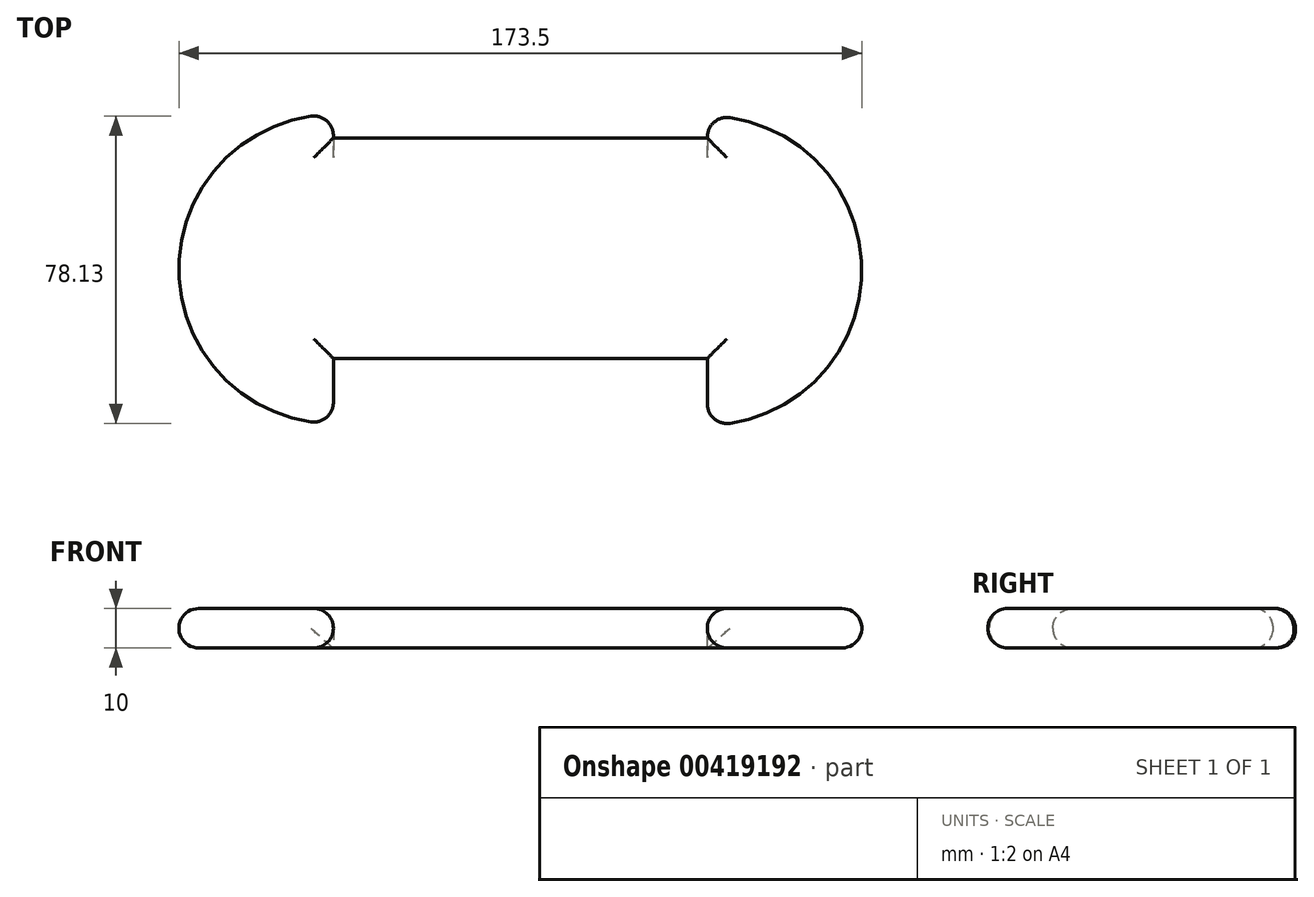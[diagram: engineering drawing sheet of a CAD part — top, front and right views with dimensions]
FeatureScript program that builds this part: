
annotation { "Feature Type Name" : "Feature", "Feature Type Description" : "" }
export const myFeature = defineFeature(function(context is Context, id is Id, definition is map)
    precondition{}
    {
        {
            var Q0;
            Q0=qCreatedBy(makeId("Top.planeOp"),FACE);
            var sketch = newSketch(context, id + "F0", { "sketchPlane" : qUnion([Q0])});
            skLineSegment(sketch, "E0.bottom", {"start": v(-45.33, 33.57) * mm, "end": v(49.67, 33.57) * mm});
            skLineSegment(sketch, "E0.top", {"start": v(-45.33, -22.43) * mm, "end": v(49.67, -22.43) * mm});
            skLineSegment(sketch, "E0.left", {"start": v(-45.33, 33.57) * mm, "end": v(-45.33, -22.43) * mm});
            skLineSegment(sketch, "E0.right", {"start": v(49.67, 33.57) * mm, "end": v(49.67, -22.43) * mm});
            skArc(sketch, "E1", {"start": v(-45.33, 39.54) * mm, "mid": v(-84.58, 0.3) * mm, "end": v(-45.33, -38.96) * mm});
            skArc(sketch, "E2", {"start": v(49.67, -39.32) * mm, "mid": v(88.92, -0.07) * mm, "end": v(49.67, 39.18) * mm});
            skLineSegment(sketch, "E3", {"start": v(-45.33, 33.57) * mm, "end": v(-45.33, 39.54) * mm});
            skLineSegment(sketch, "E4", {"start": v(-45.33, 39.54) * mm, "end": v(-45.33, -38.96) * mm});
            skLineSegment(sketch, "E5", {"start": v(49.67, 33.57) * mm, "end": v(49.67, 39.18) * mm});
            skLineSegment(sketch, "E6", {"start": v(49.67, 39.18) * mm, "end": v(49.67, -39.32) * mm});
            skSolve(sketch);
        }
        {
            var Q0;
            {var subQ0=sQuery(id+"F0.wireOp",EDGE,"E2");Q0=makeQuery(id+"F0.imprint","IMPRINT",FACE,{"disambiguationData":[TD([[makeQuery(id+"F0.imprint","IMPRINT",EDGE,{"derivedFrom":subQ0}),1.0]])]});}
            var Q1;
            {var subQ0=sQuery(id+"F0.wireOp",EDGE,"E0.bottom");Q1=makeQuery(id+"F0.imprint","IMPRINT",FACE,{"disambiguationData":[TD([[makeQuery(id+"F0.imprint","IMPRINT",EDGE,{"derivedFrom":subQ0}),-1.0]])]});}
            var Q2;
            {var subQ0=sQuery(id+"F0.wireOp",EDGE,"E1");Q2=makeQuery(id+"F0.imprint","IMPRINT",FACE,{"disambiguationData":[TD([[makeQuery(id+"F0.imprint","IMPRINT",EDGE,{"derivedFrom":subQ0}),1.0]])]});}
            extrude(context, id + "F1", {"entities" : qUnion([Q0, Q1, Q2]), "depth" : 10 * mm});
        }
        {
            var Q0;
            Q0=makeQuery(id+"F1.opExtrude","CAP_EDGE",EDGE,{"disambiguationData":[OSD([sQuery(id+"F0.wireOp",EDGE,"E1")])],"isStart":true});
            var Q1;
            Q1=makeQuery(id+"F1.opExtrude","CAP_EDGE",EDGE,{"disambiguationData":[OSD([sQuery(id+"F0.wireOp",EDGE,"E0.top")])],"isStart":true});
            var Q2;
            {var subQ0=sQuery(id+"F0.wireOp",EDGE,"E6");Q2=makeQuery(id+"F1.opExtrude","CAP_EDGE",EDGE,{"disambiguationData":[OSD([subQ0]),TDD([makeQuery(id+"F0.imprint","IMPRINT",EDGE,{"disambiguationData":[TD([[makeQuery(id+"F0.imprint","INTERSECT",VERTEX,{"derivedFrom":[sQuery(id+"F0.wireOp",EDGE,"E0.top"),subQ0]}),-1.0]])],"derivedFrom":subQ0})])],"isStart":true});}
            var Q3;
            Q3=makeQuery(id+"F1.opExtrude","CAP_EDGE",EDGE,{"disambiguationData":[OSD([sQuery(id+"F0.wireOp",EDGE,"E2")])],"isStart":true});
            var Q4;
            {var subQ0=sQuery(id+"F0.wireOp",EDGE,"E6");Q4=makeQuery(id+"F1.opExtrude","CAP_EDGE",EDGE,{"disambiguationData":[OSD([subQ0]),TDD([makeQuery(id+"F0.imprint","IMPRINT",EDGE,{"disambiguationData":[TD([[makeQuery(id+"F0.imprint","INTERSECT",VERTEX,{"derivedFrom":[sQuery(id+"F0.wireOp",EDGE,"E0.bottom"),subQ0]}),1.0]])],"derivedFrom":subQ0})])],"isStart":true});}
            var Q5;
            Q5=makeQuery(id+"F1.opExtrude","CAP_EDGE",EDGE,{"disambiguationData":[OSD([sQuery(id+"F0.wireOp",EDGE,"E0.bottom")])],"isStart":true});
            var Q6;
            {var subQ0=sQuery(id+"F0.wireOp",EDGE,"E4");Q6=makeQuery(id+"F1.opExtrude","CAP_EDGE",EDGE,{"disambiguationData":[OSD([subQ0]),TDD([makeQuery(id+"F0.imprint","IMPRINT",EDGE,{"disambiguationData":[TD([[makeQuery(id+"F0.imprint","INTERSECT",VERTEX,{"derivedFrom":[sQuery(id+"F0.wireOp",EDGE,"E0.bottom"),subQ0]}),1.0]])],"derivedFrom":subQ0})])],"isStart":true});}
            var Q7;
            {var subQ0=sQuery(id+"F0.wireOp",EDGE,"E6");var subQ1=sQuery(id+"F0.wireOp",EDGE,"E2");Q7=makeQuery(id+"F1.opExtrude","SWEPT_EDGE",EDGE,{"disambiguationData":[OSD([subQ1,subQ0]),TDD([makeQuery(id+"F0.imprint","INTERSECT",VERTEX,{"disambiguationData":[OD(0.0)],"derivedFrom":[subQ1,subQ0]})])]});}
            var Q8;
            Q8=makeQuery(id+"F1.opExtrude","CAP_EDGE",EDGE,{"disambiguationData":[OSD([sQuery(id+"F0.wireOp",EDGE,"E2")])],"isStart":false});
            var Q9;
            {var subQ0=sQuery(id+"F0.wireOp",EDGE,"E4");var subQ1=sQuery(id+"F0.wireOp",EDGE,"E1");Q9=makeQuery(id+"F1.opExtrude","SWEPT_EDGE",EDGE,{"disambiguationData":[OSD([subQ1,subQ0]),TDD([makeQuery(id+"F0.imprint","INTERSECT",VERTEX,{"disambiguationData":[OD(1.0)],"derivedFrom":[subQ1,subQ0]})])]});}
            var Q10;
            Q10=makeQuery(id+"F1.opExtrude","CAP_EDGE",EDGE,{"disambiguationData":[OSD([sQuery(id+"F0.wireOp",EDGE,"E1")])],"isStart":false});
            var Q11;
            Q11=makeQuery(id+"F1.opExtrude","CAP_EDGE",EDGE,{"disambiguationData":[OSD([sQuery(id+"F0.wireOp",EDGE,"E0.top")])],"isStart":false});
            var Q12;
            Q12=makeQuery(id+"F1.opExtrude","SWEPT_FACE",FACE,{"disambiguationData":[OSD([sQuery(id+"F0.wireOp",EDGE,"E2")])]});
            var Q13;
            Q13=makeQuery(id+"F1.opExtrude","SWEPT_FACE",FACE,{"disambiguationData":[OSD([sQuery(id+"F0.wireOp",EDGE,"E1")])]});
            var Q14;
            {var subQ0=sQuery(id+"F0.wireOp",EDGE,"E4");Q14=makeQuery(id+"F1.opExtrude","CAP_EDGE",EDGE,{"disambiguationData":[OSD([subQ0]),TDD([makeQuery(id+"F0.imprint","IMPRINT",EDGE,{"disambiguationData":[TD([[makeQuery(id+"F0.imprint","INTERSECT",VERTEX,{"derivedFrom":[sQuery(id+"F0.wireOp",EDGE,"E0.top"),subQ0]}),-1.0]])],"derivedFrom":subQ0})])],"isStart":true});}
            fillet(context, id + "F2", {"entities" : qUnion([Q0, Q1, Q2, Q3, Q4, Q5, Q6, Q7, Q8, Q9, Q10, Q11, Q12, Q13, Q14]), "radius" : 5 * mm, "tangentPropagation" : true, "allowEdgeOverflow" : false});
        }
        {
            var Q0;
            Q0=makeQuery(id+"F1.opExtrude","CAP_EDGE",EDGE,{"disambiguationData":[OSD([sQuery(id+"F0.wireOp",EDGE,"E0.bottom")])],"isStart":false});
            var Q1;
            {var subQ0=sQuery(id+"F0.wireOp",EDGE,"E4");Q1=makeQuery(id+"F1.opExtrude","CAP_EDGE",EDGE,{"disambiguationData":[OSD([subQ0]),TDD([makeQuery(id+"F0.imprint","IMPRINT",EDGE,{"disambiguationData":[TD([[makeQuery(id+"F0.imprint","INTERSECT",VERTEX,{"derivedFrom":[sQuery(id+"F0.wireOp",EDGE,"E0.bottom"),subQ0]}),1.0]])],"derivedFrom":subQ0})])],"isStart":false});}
            var Q2;
            {var subQ0=sQuery(id+"F0.wireOp",EDGE,"E4");Q2=makeQuery(id+"F1.opExtrude","CAP_EDGE",EDGE,{"disambiguationData":[OSD([subQ0]),TDD([makeQuery(id+"F0.imprint","IMPRINT",EDGE,{"disambiguationData":[TD([[makeQuery(id+"F0.imprint","INTERSECT",VERTEX,{"derivedFrom":[sQuery(id+"F0.wireOp",EDGE,"E0.top"),subQ0]}),-1.0]])],"derivedFrom":subQ0})])],"isStart":false});}
            var Q3;
            Q3=makeQuery(id+"F1.opExtrude","CAP_FACE",FACE,{"disambiguationData":[OSD([sQuery(id+"F0.wireOp",EDGE,"E0.bottom"),sQuery(id+"F0.wireOp",EDGE,"E0.top"),sQuery(id+"F0.wireOp",EDGE,"E1"),sQuery(id+"F0.wireOp",EDGE,"E2"),sQuery(id+"F0.wireOp",EDGE,"E4"),sQuery(id+"F0.wireOp",EDGE,"E6")])],"isStart":false});
            var Q4;
            Q4=makeQuery(id+"F1.opExtrude","SWEPT_FACE",FACE,{"disambiguationData":[OSD([sQuery(id+"F0.wireOp",EDGE,"E2")])]});
            var Q5;
            {var subQ0=sQuery(id+"F0.wireOp",EDGE,"E2");Q5=makeQuery(id+"F2.opFillet","BLEND_EDGE",EDGE,{"blendedFrom":[makeQuery(id+"F1.opExtrude","CAP_EDGE",EDGE,{"disambiguationData":[OSD([subQ0])],"isStart":true}),makeQuery(id+"F1.opExtrude","CAP_FACE",FACE,{"disambiguationData":[OSD([sQuery(id+"F0.wireOp",EDGE,"E0.bottom"),sQuery(id+"F0.wireOp",EDGE,"E0.top"),sQuery(id+"F0.wireOp",EDGE,"E1"),subQ0,sQuery(id+"F0.wireOp",EDGE,"E4"),sQuery(id+"F0.wireOp",EDGE,"E6")])],"isStart":true})],"blendedInto":[makeQuery(id+"F1.opExtrude","CAP_FACE",FACE,{"disambiguationData":[OSD([sQuery(id+"F0.wireOp",EDGE,"E0.bottom"),sQuery(id+"F0.wireOp",EDGE,"E0.top"),sQuery(id+"F0.wireOp",EDGE,"E1"),subQ0,sQuery(id+"F0.wireOp",EDGE,"E4"),sQuery(id+"F0.wireOp",EDGE,"E6")])],"isStart":true})]});}
            var Q6;
            {var subQ0=sQuery(id+"F0.wireOp",EDGE,"E0.bottom");Q6=makeQuery(id+"F2.opFillet","BLEND_EDGE",EDGE,{"blendedFrom":[makeQuery(id+"F1.opExtrude","CAP_EDGE",EDGE,{"disambiguationData":[OSD([subQ0])],"isStart":true}),makeQuery(id+"F1.opExtrude","CAP_FACE",FACE,{"disambiguationData":[OSD([subQ0,sQuery(id+"F0.wireOp",EDGE,"E0.top"),sQuery(id+"F0.wireOp",EDGE,"E1"),sQuery(id+"F0.wireOp",EDGE,"E2"),sQuery(id+"F0.wireOp",EDGE,"E4"),sQuery(id+"F0.wireOp",EDGE,"E6")])],"isStart":true})],"blendedInto":[makeQuery(id+"F1.opExtrude","CAP_FACE",FACE,{"disambiguationData":[OSD([subQ0,sQuery(id+"F0.wireOp",EDGE,"E0.top"),sQuery(id+"F0.wireOp",EDGE,"E1"),sQuery(id+"F0.wireOp",EDGE,"E2"),sQuery(id+"F0.wireOp",EDGE,"E4"),sQuery(id+"F0.wireOp",EDGE,"E6")])],"isStart":true})]});}
            var Q7;
            {var subQ0=sQuery(id+"F0.wireOp",EDGE,"E6");var subQ1=sQuery(id+"F0.wireOp",EDGE,"E2");var subQ2=sQuery(id+"F0.wireOp",EDGE,"E0.bottom");Q7=makeQuery(id+"F2.opFillet","BLEND_EDGE",EDGE,{"blendedFrom":[makeQuery(id+"F1.opExtrude","CAP_EDGE",EDGE,{"disambiguationData":[OSD([subQ0]),TDD([makeQuery(id+"F0.imprint","IMPRINT",EDGE,{"disambiguationData":[TD([[makeQuery(id+"F0.imprint","INTERSECT",VERTEX,{"derivedFrom":[subQ2,subQ0]}),1.0]])],"derivedFrom":subQ0})])],"isStart":true}),makeQuery(id+"F1.opExtrude","CAP_FACE",FACE,{"disambiguationData":[OSD([subQ2,sQuery(id+"F0.wireOp",EDGE,"E0.top"),sQuery(id+"F0.wireOp",EDGE,"E1"),subQ1,sQuery(id+"F0.wireOp",EDGE,"E4"),subQ0])],"isStart":true})],"blendedInto":[makeQuery(id+"F1.opExtrude","CAP_FACE",FACE,{"disambiguationData":[OSD([subQ2,sQuery(id+"F0.wireOp",EDGE,"E0.top"),sQuery(id+"F0.wireOp",EDGE,"E1"),subQ1,sQuery(id+"F0.wireOp",EDGE,"E4"),subQ0])],"isStart":true})]});}
            fillet(context, id + "F3", {"entities" : qUnion([Q0, Q1, Q2, Q3, Q4, Q5, Q6, Q7]), "radius" : 5 * mm, "tangentPropagation" : true, "allowEdgeOverflow" : false});
        }
    });
